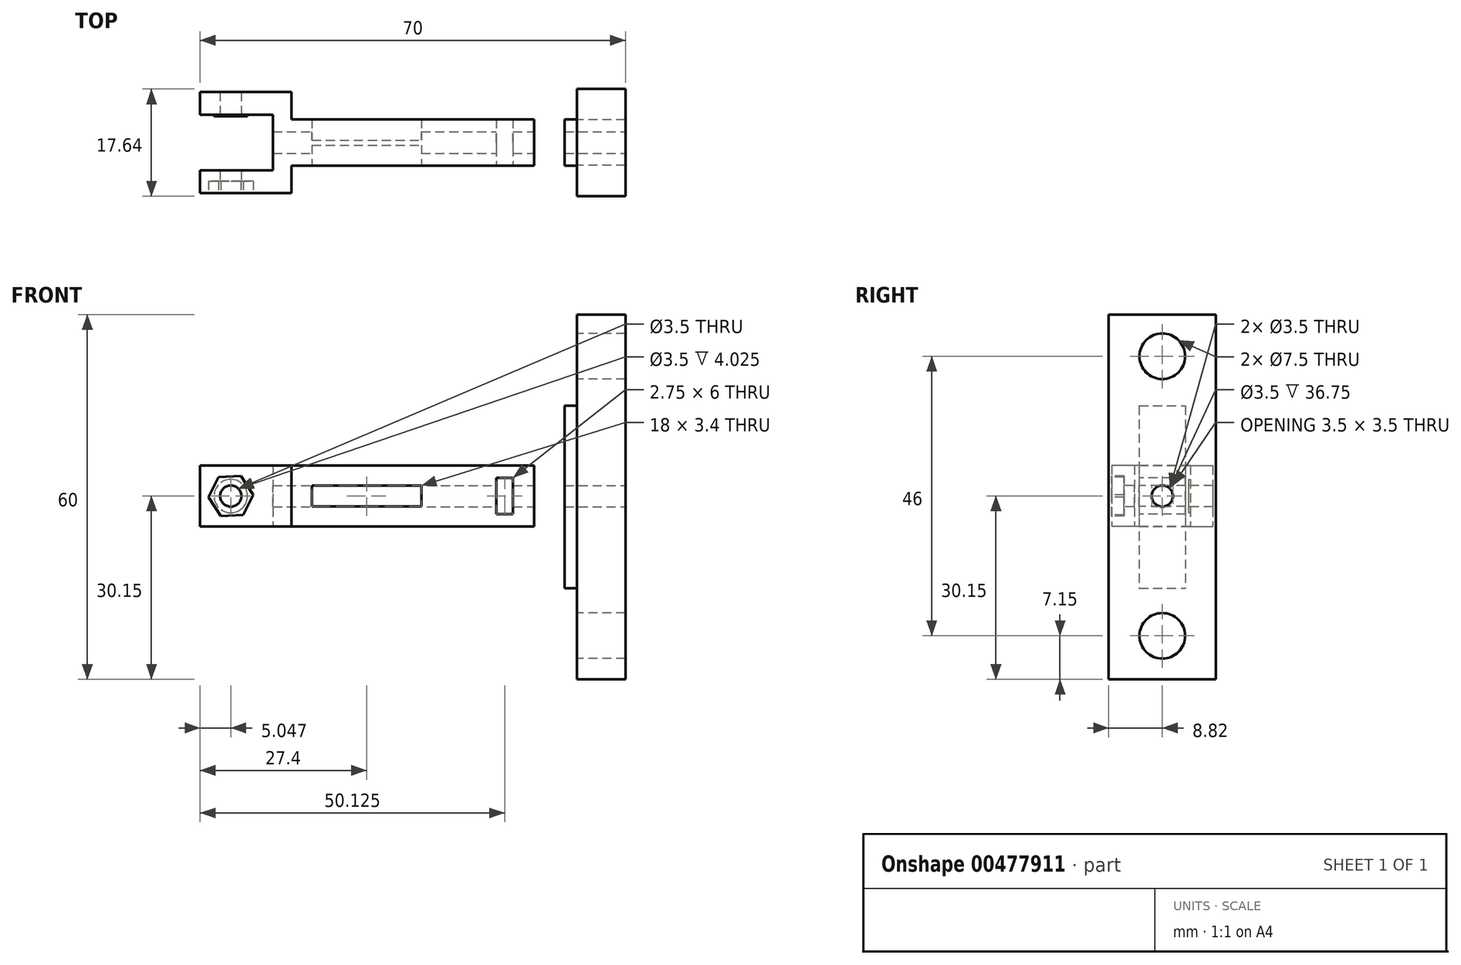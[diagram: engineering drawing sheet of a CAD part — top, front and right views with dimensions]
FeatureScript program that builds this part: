
annotation { "Feature Type Name" : "Feature", "Feature Type Description" : "" }
export const myFeature = defineFeature(function(context is Context, id is Id, definition is map)
    precondition{}
    {
        {
            var Q0;
            Q0=qCreatedBy(makeId("Top.planeOp"),FACE);
            var sketch = newSketch(context, id + "F0", { "sketchPlane" : qUnion([Q0])});
            skLineSegment(sketch, "E0.bottom", {"start": v(0, 0) * mm, "end": v(40, 0) * mm});
            skLineSegment(sketch, "E0.top", {"start": v(0, -3.83) * mm, "end": v(40, -3.83) * mm});
            skLineSegment(sketch, "E0.left", {"start": v(0, 0) * mm, "end": v(0, -3.83) * mm});
            skLineSegment(sketch, "E0.right", {"start": v(40, 0) * mm, "end": v(40, -3.83) * mm});
            skLineSegment(sketch, "E1.bottom", {"start": v(-3, 0) * mm, "end": v(0, 0) * mm});
            skLineSegment(sketch, "E1.top", {"start": v(-15, -8.32) * mm, "end": v(0, -8.32) * mm});
            skLineSegment(sketch, "E1.left", {"start": v(-15, -4.6) * mm, "end": v(-15, -8.32) * mm});
            skLineSegment(sketch, "E1.right", {"start": v(0, 0) * mm, "end": v(0, -8.32) * mm});
            skLineSegment(sketch, "E2.top", {"start": v(-15, -4.6) * mm, "end": v(-3, -4.6) * mm});
            skLineSegment(sketch, "E2.right", {"start": v(-3, 0) * mm, "end": v(-3, -4.6) * mm});
            skLineSegment(sketch, "E3.MirrorCS", {"start": v(0, 0) * mm, "end": v(0, 3.83) * mm});
            skLineSegment(sketch, "E4.MirrorCS", {"start": v(0, 0) * mm, "end": v(0, 8.32) * mm});
            skLineSegment(sketch, "E5.MirrorCS", {"start": v(-15, 4.6) * mm, "end": v(-15, 8.32) * mm});
            skLineSegment(sketch, "E6.MirrorCS", {"start": v(-3, 0) * mm, "end": v(-3, 4.6) * mm});
            skLineSegment(sketch, "E7.MirrorCS", {"start": v(-15, 8.32) * mm, "end": v(0, 8.32) * mm});
            skLineSegment(sketch, "E8.MirrorCS", {"start": v(-15, 4.6) * mm, "end": v(-3, 4.6) * mm});
            skLineSegment(sketch, "E9.MirrorCS", {"start": v(40, 0) * mm, "end": v(40, 3.83) * mm});
            skLineSegment(sketch, "E10.MirrorCS", {"start": v(0, 3.83) * mm, "end": v(40, 3.83) * mm});
            skSolve(sketch);
        }
        {
            var Q0;
            {var subQ2=sQuery(id+"F0.wireOp",EDGE,"E1.top");Q0=makeQuery(id+"F0.imprint","IMPRINT",FACE,{"disambiguationData":[TD([[makeQuery(id+"F0.imprint","IMPRINT",EDGE,{"derivedFrom":subQ2}),1.0]])]});}
            var Q1;
            Q1=makeQuery(id+"F0.imprint","IMPRINT",FACE,{"disambiguationData":[TD([[makeQuery(id+"F0.imprint","IMPRINT",EDGE,{"derivedFrom":sQuery(id+"F0.wireOp",EDGE,"E5.MirrorCS")}),-1.0]])]});
            var Q2;
            {var subQ0=sQuery(id+"F0.wireOp",EDGE,"E0.bottom");Q2=makeQuery(id+"F0.imprint","IMPRINT",FACE,{"disambiguationData":[TD([[makeQuery(id+"F0.imprint","IMPRINT",EDGE,{"derivedFrom":subQ0}),1.0]])]});}
            var Q3;
            {var subQ0=sQuery(id+"F0.wireOp",EDGE,"E0.bottom");Q3=makeQuery(id+"F0.imprint","IMPRINT",FACE,{"disambiguationData":[TD([[makeQuery(id+"F0.imprint","IMPRINT",EDGE,{"derivedFrom":subQ0}),-1.0]])]});}
            extrude(context, id + "F1", {"entities" : qUnion([Q0, Q1, Q2, Q3]), "depth" : 10 * mm});
        }
        {
            var Q0;
            Q0=makeQuery(id+"F1.opExtrude","SWEPT_FACE",FACE,{"disambiguationData":[OSD([sQuery(id+"F0.wireOp",EDGE,"E1.top")])]});
            var sketch = newSketch(context, id + "F2", { "sketchPlane" : qUnion([Q0])});
            skCircle(sketch, "E11", {"center": v(-9.95, 5) * mm, "radius": 1.75 * mm});
            skSolve(sketch);
        }
        {
            var Q0;
            Q0=makeQuery(id+"F2.imprint","IMPRINT",FACE,{"disambiguationData":[TD([[makeQuery(id+"F2.imprint","IMPRINT",EDGE,{"derivedFrom":sQuery(id+"F2.wireOp",EDGE,"E11")}),1.0]])]});
            extrude(context, id + "F3", {"entities" : qUnion([Q0]), "operationType" : NewBodyOperationType.REMOVE, "endBound" : BoundingType.THROUGH_ALL, "oppositeDirection" : true, "depth" : 25 * mm});
        }
        {
            var Q0;
            Q0=makeQuery(id+"F1.opExtrude","SWEPT_FACE",FACE,{"disambiguationData":[OSD([sQuery(id+"F0.wireOp",EDGE,"E0.top")])]});
            var sketch = newSketch(context, id + "F4", { "sketchPlane" : qUnion([Q0])});
            skLineSegment(sketch, "E12.bottom", {"start": v(3.4, 3.3) * mm, "end": v(21.4, 3.3) * mm});
            skLineSegment(sketch, "E12.top", {"start": v(3.4, 6.7) * mm, "end": v(21.4, 6.7) * mm});
            skLineSegment(sketch, "E12.left", {"start": v(3.4, 3.3) * mm, "end": v(3.4, 6.7) * mm});
            skLineSegment(sketch, "E12.right", {"start": v(21.4, 3.3) * mm, "end": v(21.4, 6.7) * mm});
            skLineSegment(sketch, "E13.bottom", {"start": v(33.75, 8) * mm, "end": v(36.5, 8) * mm});
            skLineSegment(sketch, "E13.top", {"start": v(33.75, 2) * mm, "end": v(36.5, 2) * mm});
            skLineSegment(sketch, "E13.left", {"start": v(33.75, 8) * mm, "end": v(33.75, 2) * mm});
            skLineSegment(sketch, "E13.right", {"start": v(36.5, 8) * mm, "end": v(36.5, 2) * mm});
            skSolve(sketch);
        }
        {
            var Q0;
            Q0=makeQuery(id+"F4.imprint","IMPRINT",FACE,{"disambiguationData":[TD([[makeQuery(id+"F4.imprint","IMPRINT",EDGE,{"derivedFrom":sQuery(id+"F4.wireOp",EDGE,"E12.bottom")}),1.0]])]});
            var Q1;
            Q1=makeQuery(id+"F4.imprint","IMPRINT",FACE,{"disambiguationData":[TD([[makeQuery(id+"F4.imprint","IMPRINT",EDGE,{"derivedFrom":sQuery(id+"F4.wireOp",EDGE,"E13.bottom")}),-1.0]])]});
            extrude(context, id + "F5", {"entities" : qUnion([Q0, Q1]), "operationType" : NewBodyOperationType.REMOVE, "endBound" : BoundingType.THROUGH_ALL, "oppositeDirection" : true, "depth" : 25 * mm});
        }
        {
            var Q0;
            Q0=makeQuery(id+"F1.opExtrude","SWEPT_FACE",FACE,{"disambiguationData":[OSD([sQuery(id+"F0.wireOp",EDGE,"E0.right"),sQuery(id+"F0.wireOp",EDGE,"E9.MirrorCS")])]});
            var sketch = newSketch(context, id + "F6", { "sketchPlane" : qUnion([Q0])});
            skCircle(sketch, "E14", {"center": v(0, 5) * mm, "radius": 1.75 * mm});
            skSolve(sketch);
        }
        {
            var Q0;
            Q0=makeQuery(id+"F6.imprint","IMPRINT",FACE,{"disambiguationData":[TD([[makeQuery(id+"F6.imprint","IMPRINT",EDGE,{"derivedFrom":sQuery(id+"F6.wireOp",EDGE,"E14")}),1.0]])]});
            extrude(context, id + "F7", {"entities" : qUnion([Q0]), "operationType" : NewBodyOperationType.REMOVE, "oppositeDirection" : true, "depth" : 15 * mm});
        }
        {
            var Q0;
            Q0=makeQuery(id+"F1.opExtrude","SWEPT_FACE",FACE,{"disambiguationData":[OSD([sQuery(id+"F0.wireOp",EDGE,"E0.right"),sQuery(id+"F0.wireOp",EDGE,"E9.MirrorCS")])]});
            cPlane(context, id + "F8", {"entities" : qUnion([Q0]), "cplaneType" : CPlaneType.OFFSET, "offset" : 5 * mm, "width" : 150 * mm, "height" : 150 * mm});
        }
        {
            var Q0;
            Q0=qCreatedBy(id+"F8.planeOp",FACE);
            var sketch = newSketch(context, id + "F9", { "sketchPlane" : qUnion([Q0])});
            skLineSegment(sketch, "E15.0", {"start": v(3.83, 10) * mm, "end": v(3.83, 0) * mm});
            skLineSegment(sketch, "E16.0", {"start": v(-3.82, 10) * mm, "end": v(-3.82, 0) * mm});
            skLineSegment(sketch, "E17.bottom", {"start": v(-3.82, 19.85) * mm, "end": v(3.83, 19.85) * mm});
            skLineSegment(sketch, "E17.top", {"start": v(-3.82, -10.15) * mm, "end": v(3.83, -10.15) * mm});
            skLineSegment(sketch, "E17.left", {"start": v(-3.82, 19.85) * mm, "end": v(-3.82, -10.15) * mm});
            skLineSegment(sketch, "E17.right", {"start": v(3.83, 19.85) * mm, "end": v(3.83, -10.15) * mm});
            skPoint(sketch, "E18.oppositeSnap0", {"position": v(3.83, 4.85) * mm});
            skLineSegment(sketch, "E18.bottom", {"start": v(3.83, 4.85) * mm, "end": v(3.83, 4.85) * mm});
            skLineSegment(sketch, "E18.top", {"start": v(3.83, 4.85) * mm, "end": v(3.83, 4.85) * mm});
            skLineSegment(sketch, "E18.left", {"start": v(3.83, 4.85) * mm, "end": v(3.83, 4.85) * mm});
            skLineSegment(sketch, "E18.right", {"start": v(3.83, 4.85) * mm, "end": v(3.83, 4.85) * mm});
            skSolve(sketch);
        }
        {
            var Q0;
            {var subQ0=sQuery(id+"F9.wireOp",EDGE,"E17.bottom");Q0=makeQuery(id+"F9.imprint","IMPRINT",FACE,{"disambiguationData":[TD([[makeQuery(id+"F9.imprint","IMPRINT",EDGE,{"derivedFrom":subQ0}),-1.0]])]});}
            extrude(context, id + "F10", {"entities" : qUnion([Q0]), "depth" : 2 * mm});
        }
        {
            var Q0;
            Q0=makeQuery(id+"F10.opExtrude","CAP_FACE",FACE,{"disambiguationData":[OSD([sQuery(id+"F9.wireOp",EDGE,"E17.bottom"),sQuery(id+"F9.wireOp",EDGE,"E17.top"),sQuery(id+"F9.wireOp",EDGE,"E17.left"),sQuery(id+"F9.wireOp",EDGE,"E17.right")])],"isStart":false});
            var sketch = newSketch(context, id + "F11", { "sketchPlane" : qUnion([Q0])});
            skLineSegment(sketch, "E19.bottom", {"start": v(8.82, 34.85) * mm, "end": v(-8.83, 34.85) * mm});
            skLineSegment(sketch, "E19.top", {"start": v(8.83, -25.15) * mm, "end": v(-8.82, -25.15) * mm});
            skLineSegment(sketch, "E19.left", {"start": v(8.82, 34.85) * mm, "end": v(8.83, -25.15) * mm});
            skLineSegment(sketch, "E19.right", {"start": v(-8.83, 34.85) * mm, "end": v(-8.82, -25.15) * mm});
            skSolve(sketch);
        }
        {
            var Q0;
            Q0=qSketchRegion(id+"F11",true);
            extrude(context, id + "F12", {"entities" : qUnion([Q0]), "operationType" : NewBodyOperationType.ADD, "depth" : 8 * mm});
        }
        {
            var Q0;
            Q0=makeQuery(id+"F12.opExtrude","CAP_FACE",FACE,{"disambiguationData":[OSD([sQuery(id+"F11.wireOp",EDGE,"E19.bottom"),sQuery(id+"F11.wireOp",EDGE,"E19.top"),sQuery(id+"F11.wireOp",EDGE,"E19.left"),sQuery(id+"F11.wireOp",EDGE,"E19.right")])],"isStart":false});
            var sketch = newSketch(context, id + "F13", { "sketchPlane" : qUnion([Q0])});
            skCircle(sketch, "E20.0", {"center": v(0, 5) * mm, "radius": 1.75 * mm});
            skSolve(sketch);
        }
        {
            var Q0;
            Q0=makeQuery(id+"F13.imprint","IMPRINT",FACE,{"disambiguationData":[TD([[makeQuery(id+"F13.imprint","IMPRINT",EDGE,{"derivedFrom":sQuery(id+"F13.wireOp",EDGE,"E20.0")}),1.0]])]});
            extrude(context, id + "F14", {"entities" : qUnion([Q0]), "operationType" : NewBodyOperationType.REMOVE, "endBound" : BoundingType.THROUGH_ALL, "oppositeDirection" : true, "depth" : 25 * mm});
        }
        {
            var Q0;
            Q0=makeQuery(id+"F1.opExtrude","SWEPT_FACE",FACE,{"disambiguationData":[OSD([sQuery(id+"F0.wireOp",EDGE,"E8.MirrorCS")])]});
            var sketch = newSketch(context, id + "F15", { "sketchPlane" : qUnion([Q0])});
            skCircle(sketch, "E21", {"center": v(-9.95, 5) * mm, "radius": 1.75 * mm});
            skCircle(sketch, "E22", {"center": v(-9.95, 5) * mm, "radius": 2.75 * mm});
            skSolve(sketch);
        }
        {
            var Q0;
            Q0=makeQuery(id+"F15.imprint","IMPRINT",FACE,{"disambiguationData":[TD([[makeQuery(id+"F15.imprint","IMPRINT",EDGE,{"derivedFrom":sQuery(id+"F15.wireOp",EDGE,"E21")}),1.0]])]});
            extrude(context, id + "F16", {"entities" : qUnion([Q0]), "operationType" : NewBodyOperationType.ADD, "depth" : 0.3 * mm});
        }
        {
            var Q0;
            Q0=makeQuery(id+"F1.opExtrude","SWEPT_FACE",FACE,{"disambiguationData":[OSD([sQuery(id+"F0.wireOp",EDGE,"E1.top")])]});
            var sketch = newSketch(context, id + "F17", { "sketchPlane" : qUnion([Q0])});
            skCircle(sketch, "E23.cCircle", {"center": v(-9.95, 5) * mm, "radius": 3.2 * mm, "construction": true});
            skLineSegment(sketch, "E23.0", {"start": v(-6.26, 5.2) * mm, "end": v(-7.93, 1.9) * mm});
            skLineSegment(sketch, "E23.1", {"start": v(-7.93, 1.9) * mm, "end": v(-11.62, 1.7) * mm});
            skLineSegment(sketch, "E23.2", {"start": v(-11.62, 1.7) * mm, "end": v(-13.64, 4.8) * mm});
            skLineSegment(sketch, "E23.3", {"start": v(-13.64, 4.8) * mm, "end": v(-11.98, 8.1) * mm});
            skLineSegment(sketch, "E23.4", {"start": v(-11.98, 8.1) * mm, "end": v(-8.29, 8.3) * mm});
            skLineSegment(sketch, "E23.5", {"start": v(-8.29, 8.3) * mm, "end": v(-6.26, 5.2) * mm});
            skPoint(sketch, "E23.0.midPoint", {"position": v(-7.1, 3.56) * mm});
            skSolve(sketch);
        }
        {
            var Q0;
            Q0=makeQuery(id+"F17.imprint","IMPRINT",FACE,{"disambiguationData":[TD([[makeQuery(id+"F17.imprint","IMPRINT",EDGE,{"derivedFrom":sQuery(id+"F17.wireOp",EDGE,"E23.0")}),-1.0]])]});
            extrude(context, id + "F18", {"entities" : qUnion([Q0]), "operationType" : NewBodyOperationType.REMOVE, "oppositeDirection" : true, "depth" : 2 * mm});
        }
        {
            var Q0;
            Q0=makeQuery(id+"F12.opExtrude","CAP_FACE",FACE,{"disambiguationData":[OSD([sQuery(id+"F11.wireOp",EDGE,"E19.bottom"),sQuery(id+"F11.wireOp",EDGE,"E19.top"),sQuery(id+"F11.wireOp",EDGE,"E19.left"),sQuery(id+"F11.wireOp",EDGE,"E19.right")])],"isStart":true});
            var sketch = newSketch(context, id + "F19", { "sketchPlane" : qUnion([Q0])});
            skCircle(sketch, "E24.0", {"center": v(0, 5) * mm, "radius": 1.75 * mm});
            skCircle(sketch, "E25", {"center": v(0, -18) * mm, "radius": 3.75 * mm});
            skCircle(sketch, "E26", {"center": v(0, 28) * mm, "radius": 3.75 * mm});
            skSolve(sketch);
        }
        {
            var Q0;
            Q0=makeQuery(id+"F19.imprint","IMPRINT",FACE,{"disambiguationData":[TD([[makeQuery(id+"F19.imprint","IMPRINT",EDGE,{"derivedFrom":sQuery(id+"F19.wireOp",EDGE,"E26")}),1.0]])]});
            var Q1;
            Q1=makeQuery(id+"F19.imprint","IMPRINT",FACE,{"disambiguationData":[TD([[makeQuery(id+"F19.imprint","IMPRINT",EDGE,{"derivedFrom":sQuery(id+"F19.wireOp",EDGE,"E25")}),1.0]])]});
            extrude(context, id + "F20", {"entities" : qUnion([Q0, Q1]), "operationType" : NewBodyOperationType.REMOVE, "oppositeDirection" : true, "depth" : 15 * mm});
        }
    });
